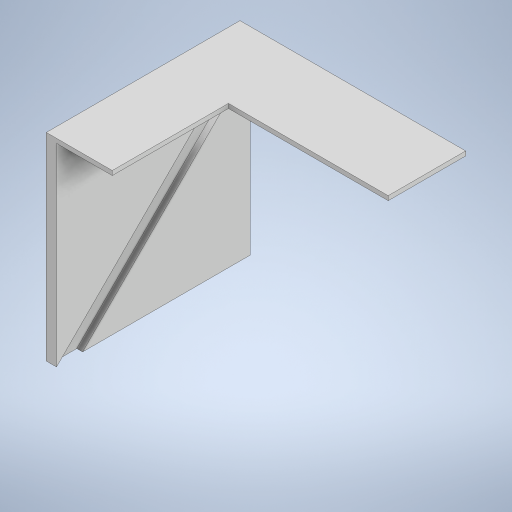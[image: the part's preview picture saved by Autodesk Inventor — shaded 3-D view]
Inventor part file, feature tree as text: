
AUTODESK INVENTOR PART (.ipt)
format: ipt  version: 2024 (Build 280153000, 153)  size: 331,776 bytes
history: native  units: mm
features: extrude x11, sketch x11
ambient origin geometry x8: Origin, YZ Plane, XZ Plane, XY Plane, X Axis, Y Axis, Z Axis, Center Point
bodies: Solid1 (feature_tree)
feature tree (22):
  extrude  "Top"  Depth=160.0mm
  extrude  "Right"  Depth=179.5mm
  extrude  "Left"  Depth=215.9mm
  extrude  "Plexiglass Cut"  Depth=25.4mm
  extrude  "Bottom"  Depth=50.8mm TaperAngle=0.0deg
  extrude  "Top Flattening"  Depth=50.8mm TaperAngle=0.0deg
  extrude  "Outer Side Flattening"  Depth=12.7mm TaperAngle=0.0deg
  extrude  "Bottom Flattening"  Depth=22.4mm TaperAngle=0.0deg
  extrude  "Inner Flattening"  Depth=22.389425mm
  extrude  "Bottom Cut"  Depth=22.4mm TaperAngle=0.0deg
  extrude  "Quarter Cut"  Depth=22.4mm TaperAngle=0.0deg
  sketch  "Sketch1"  dims[d11=220.0mm d12=160.0mm]
  sketch  "Sketch3"  dims[d15=248.6mm d16=179.5mm]
  sketch  "Sketch4"  dims[d18=304.8mm d19=215.9mm]
  sketch  "Sketch5"  dims[d20=25.4mm d21=0.0mm d22=25.4mm]
  sketch  "Sketch6"  dims[d25=266.7mm d26=50.8mm d27=0.0mm]
  sketch  "Sketch9"  dims[d28=266.7mm d29=50.8mm d30=0.0mm]
  sketch  "Sketch10"  dims[d31=12.7mm d32=304.8mm d33=0.0mm]
  sketch  "Sketch11"  dims[d34=25.4mm d35=0.0mm d46=22.4mm d47=0.0mm]
  sketch  "Sketch12"  dims[d48=22.389425mm d49=22.389425mm]
  sketch  "Sketch13"  dims[d50=0.0mm d51=0.0mm d52=22.4mm d53=0.0mm]
  sketch  "Sketch14"  dims[d54=296.8mm d55=22.4mm d56=0.0mm d57=0.0mm d58=0.0mm d59=0.0mm d60=0.0mm]
